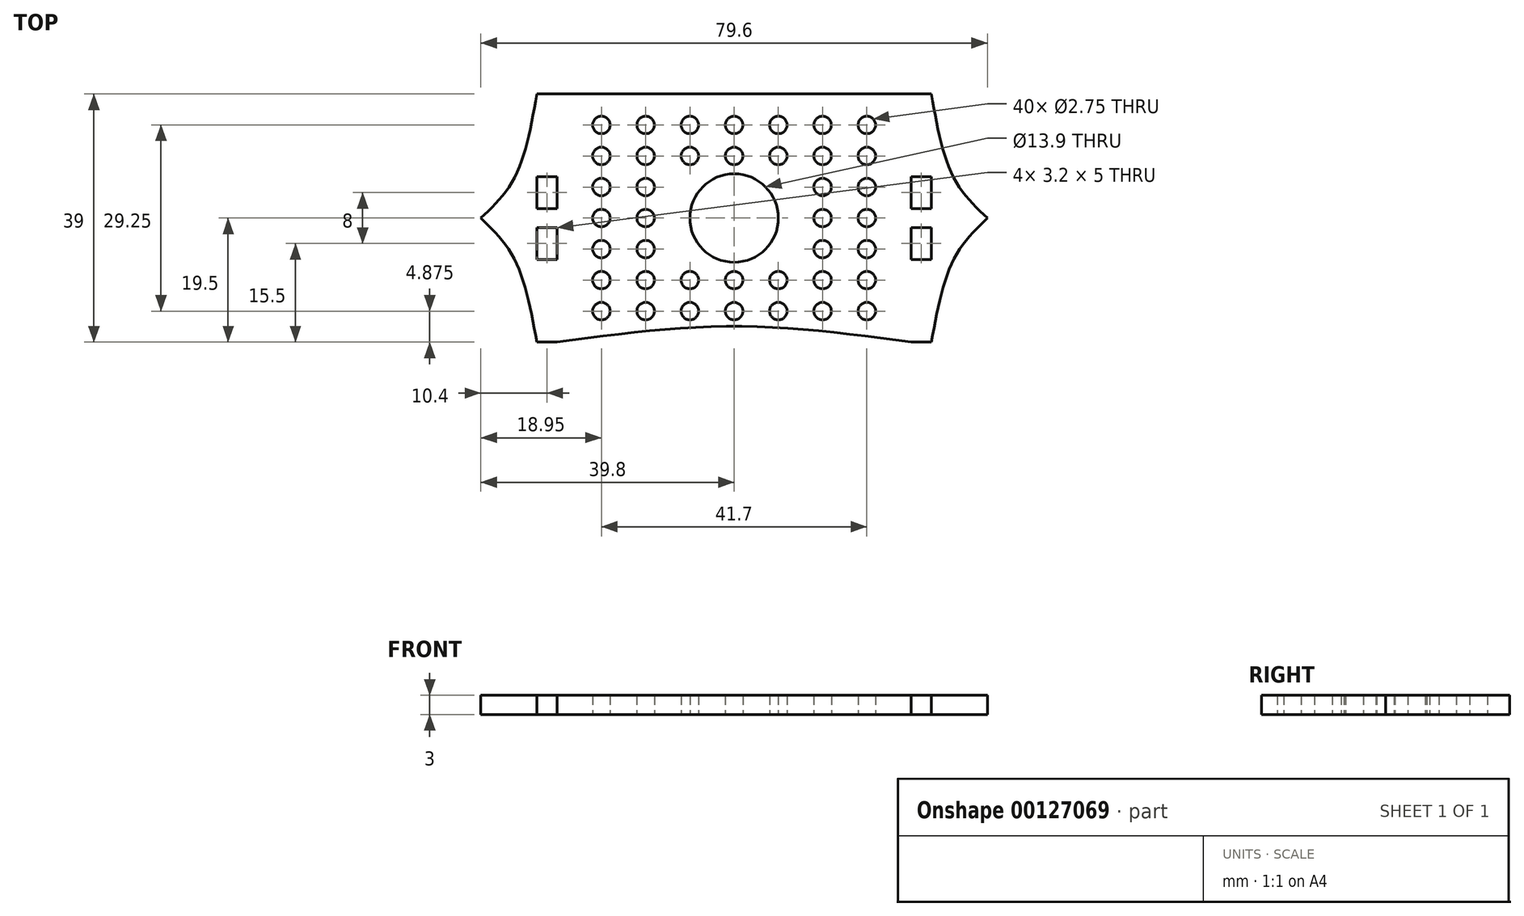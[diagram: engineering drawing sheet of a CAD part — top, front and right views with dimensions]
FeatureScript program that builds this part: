
annotation { "Feature Type Name" : "Feature", "Feature Type Description" : "" }
export const myFeature = defineFeature(function(context is Context, id is Id, definition is map)
    precondition{}
    {
        {
            var Q0;
            Q0=qCreatedBy(makeId("Top.planeOp"),FACE);
            var sketch = newSketch(context, id + "F0", { "sketchPlane" : qUnion([Q0])});
            skLineSegment(sketch, "E0", {"start": v(-27.8, -19.5) * mm, "end": v(-31, -19.5) * mm});
            skLineSegment(sketch, "E1", {"start": v(-27.8, -6.5) * mm, "end": v(-27.8, 1.84) * mm});
            skLineSegment(sketch, "E2", {"start": v(27.8, 6.5) * mm, "end": v(27.8, 3.3) * mm});
            skLineSegment(sketch, "E3", {"start": v(31, -19.5) * mm, "end": v(27.8, -19.5) * mm});
            skLineSegment(sketch, "E4", {"start": v(-27.8, -19.5) * mm, "end": v(-27.8, 1.84) * mm, "construction": true});
            skLineSegment(sketch, "E5", {"start": v(27.8, -19.5) * mm, "end": v(27.8, -3.3) * mm, "construction": true});
            skLineSegment(sketch, "E6", {"start": v(-27.8, 19.5) * mm, "end": v(-31, 19.5) * mm});
            skLineSegment(sketch, "E7", {"start": v(27.8, 19.5) * mm, "end": v(31, 19.5) * mm});
            skLineSegment(sketch, "E8", {"start": v(-31, -7) * mm, "end": v(-33.5, -7) * mm, "construction": true});
            skLineSegment(sketch, "E9", {"start": v(-27.8, 19.5) * mm, "end": v(27.8, 19.5) * mm});
            skFitSpline(sketch, "E10", {"points": [v(-27.8, -19.5) * mm, v(0, -17) * mm, v(27.8, -19.5) * mm], "startDerivative": vector(55.6, 7.5) * mm, "endDerivative": vector(55.6, -7.5) * mm});
            skLineSegment(sketch, "E11", {"start": v(-27.8, 19.5) * mm, "end": v(-13.9, 19.5) * mm, "construction": true});
            skLineSegment(sketch, "E12", {"start": v(-13.9, 19.5) * mm, "end": v(0, 19.5) * mm, "construction": true});
            skLineSegment(sketch, "E13", {"start": v(0, 19.5) * mm, "end": v(13.9, 19.5) * mm, "construction": true});
            skLineSegment(sketch, "E14", {"start": v(13.9, 19.5) * mm, "end": v(27.8, 19.5) * mm, "construction": true});
            skLineSegment(sketch, "E15", {"start": v(0, 19.5) * mm, "end": v(0, -17) * mm, "construction": true});
            skLineSegment(sketch, "E16", {"start": v(-27.8, 0) * mm, "end": v(27.8, 0) * mm, "construction": true});
            skLineSegment(sketch, "E17", {"start": v(-13.9, 19.5) * mm, "end": v(-13.9, -17.78) * mm, "construction": true});
            skLineSegment(sketch, "E18", {"start": v(13.9, 19.5) * mm, "end": v(13.9, -17.78) * mm, "construction": true});
            skLineSegment(sketch, "E19", {"start": v(20.85, 19.5) * mm, "end": v(20.85, -18.58) * mm, "construction": true});
            skLineSegment(sketch, "E20", {"start": v(6.95, 19.5) * mm, "end": v(6.95, -17.21) * mm, "construction": true});
            skLineSegment(sketch, "E21", {"start": v(-6.95, 19.5) * mm, "end": v(-6.95, -17.21) * mm, "construction": true});
            skLineSegment(sketch, "E22", {"start": v(-20.85, 19.5) * mm, "end": v(-20.85, -18.58) * mm, "construction": true});
            skCircle(sketch, "E23", {"center": v(0, 0) * mm, "radius": 6.95 * mm});
            skLineSegment(sketch, "E24", {"start": v(-27.8, 19.5) * mm, "end": v(-27.8, 9.75) * mm, "construction": true});
            skLineSegment(sketch, "E25", {"start": v(-27.8, 9.75) * mm, "end": v(27.8, 9.75) * mm, "construction": true});
            skLineSegment(sketch, "E26", {"start": v(-27.8, 0) * mm, "end": v(-27.8, -9.75) * mm, "construction": true});
            skLineSegment(sketch, "E27", {"start": v(-27.8, -9.75) * mm, "end": v(27.8, -9.75) * mm, "construction": true});
            skLineSegment(sketch, "E28", {"start": v(-27.8, 14.63) * mm, "end": v(27.8, 14.63) * mm, "construction": true});
            skLineSegment(sketch, "E29", {"start": v(-27.8, -4.88) * mm, "end": v(27.8, -4.87) * mm, "construction": true});
            skLineSegment(sketch, "E30", {"start": v(-27.8, 9.75) * mm, "end": v(-27.8, 4.88) * mm, "construction": true});
            skLineSegment(sketch, "E31", {"start": v(-27.8, 4.88) * mm, "end": v(27.8, 4.88) * mm, "construction": true});
            skLineSegment(sketch, "E32", {"start": v(-27.8, -9.75) * mm, "end": v(-27.8, -14.62) * mm, "construction": true});
            skLineSegment(sketch, "E33", {"start": v(-27.8, -14.62) * mm, "end": v(27.8, -14.62) * mm, "construction": true});
            skCircle(sketch, "E34", {"center": v(-20.85, -14.62) * mm, "radius": 1.38 * mm});
            skCircle(sketch, "E35", {"center": v(-13.9, -14.62) * mm, "radius": 1.38 * mm});
            skCircle(sketch, "E36", {"center": v(-6.95, -14.62) * mm, "radius": 1.38 * mm});
            skCircle(sketch, "E37", {"center": v(0, -14.62) * mm, "radius": 1.38 * mm});
            skCircle(sketch, "E38", {"center": v(-20.85, -9.75) * mm, "radius": 1.38 * mm});
            skCircle(sketch, "E39", {"center": v(-13.9, -9.75) * mm, "radius": 1.38 * mm});
            skCircle(sketch, "E40", {"center": v(-6.95, -9.75) * mm, "radius": 1.38 * mm});
            skCircle(sketch, "E41", {"center": v(0, -9.75) * mm, "radius": 1.38 * mm});
            skCircle(sketch, "E42", {"center": v(-20.85, -4.88) * mm, "radius": 1.38 * mm});
            skCircle(sketch, "E43", {"center": v(-13.9, -4.88) * mm, "radius": 1.38 * mm});
            skCircle(sketch, "E44", {"center": v(-20.85, 0) * mm, "radius": 1.38 * mm});
            skCircle(sketch, "E45", {"center": v(-13.9, 0) * mm, "radius": 1.38 * mm});
            skCircle(sketch, "E46.MirrorC", {"center": v(6.95, -9.75) * mm, "radius": 1.38 * mm});
            skCircle(sketch, "E47.MirrorC", {"center": v(20.85, -9.75) * mm, "radius": 1.38 * mm});
            skCircle(sketch, "E48.MirrorC", {"center": v(13.9, -14.62) * mm, "radius": 1.38 * mm});
            skCircle(sketch, "E49.MirrorC", {"center": v(13.9, -9.75) * mm, "radius": 1.38 * mm});
            skCircle(sketch, "E50.MirrorC", {"center": v(20.85, -14.62) * mm, "radius": 1.38 * mm});
            skCircle(sketch, "E51.MirrorC", {"center": v(6.95, -14.62) * mm, "radius": 1.38 * mm});
            skLineSegment(sketch, "E52.MirrorCS", {"start": v(27.8, -4.87) * mm, "end": v(-27.8, -4.88) * mm, "construction": true});
            skCircle(sketch, "E53.MirrorC", {"center": v(20.85, 0) * mm, "radius": 1.38 * mm});
            skCircle(sketch, "E54.MirrorC", {"center": v(20.85, -4.88) * mm, "radius": 1.38 * mm});
            skCircle(sketch, "E55.MirrorC", {"center": v(13.9, 0) * mm, "radius": 1.38 * mm});
            skCircle(sketch, "E56.MirrorC", {"center": v(13.9, -4.88) * mm, "radius": 1.38 * mm});
            skLineSegment(sketch, "E57.MirrorCS", {"start": v(27.8, 0) * mm, "end": v(-27.8, 0) * mm, "construction": true});
            skCircle(sketch, "E58.MirrorC", {"center": v(6.95, 14.62) * mm, "radius": 1.38 * mm});
            skCircle(sketch, "E59.MirrorC", {"center": v(-13.9, 14.63) * mm, "radius": 1.38 * mm});
            skCircle(sketch, "E60.MirrorC", {"center": v(20.85, 9.75) * mm, "radius": 1.38 * mm});
            skCircle(sketch, "E61.MirrorC", {"center": v(-13.9, 9.75) * mm, "radius": 1.38 * mm});
            skCircle(sketch, "E62.MirrorC", {"center": v(-20.85, 9.75) * mm, "radius": 1.38 * mm});
            skCircle(sketch, "E63.MirrorC", {"center": v(13.9, 9.75) * mm, "radius": 1.38 * mm});
            skCircle(sketch, "E64.MirrorC", {"center": v(13.9, 14.62) * mm, "radius": 1.38 * mm});
            skCircle(sketch, "E65.MirrorC", {"center": v(6.95, 9.75) * mm, "radius": 1.38 * mm});
            skCircle(sketch, "E66.MirrorC", {"center": v(20.85, 14.62) * mm, "radius": 1.38 * mm});
            skCircle(sketch, "E67.MirrorC", {"center": v(0, 9.75) * mm, "radius": 1.38 * mm});
            skCircle(sketch, "E68.MirrorC", {"center": v(-6.95, 9.75) * mm, "radius": 1.38 * mm});
            skCircle(sketch, "E69.MirrorC", {"center": v(-6.95, 14.63) * mm, "radius": 1.38 * mm});
            skCircle(sketch, "E70.MirrorC", {"center": v(-20.85, 14.63) * mm, "radius": 1.38 * mm});
            skCircle(sketch, "E71.MirrorC", {"center": v(0, 14.62) * mm, "radius": 1.38 * mm});
            skLineSegment(sketch, "E72.MirrorCS", {"start": v(27.8, 4.88) * mm, "end": v(-27.8, 4.87) * mm, "construction": true});
            skLineSegment(sketch, "E73.MirrorCS", {"start": v(20.85, -19.5) * mm, "end": v(20.85, 18.58) * mm, "construction": true});
            skLineSegment(sketch, "E74.MirrorCS", {"start": v(13.9, -19.5) * mm, "end": v(13.9, 17.78) * mm, "construction": true});
            skCircle(sketch, "E75.MirrorC", {"center": v(13.9, 4.88) * mm, "radius": 1.38 * mm});
            skCircle(sketch, "E76.MirrorC", {"center": v(20.85, 4.87) * mm, "radius": 1.38 * mm});
            skLineSegment(sketch, "E77.MirrorCS", {"start": v(-27.8, 4.87) * mm, "end": v(27.8, 4.88) * mm, "construction": true});
            skCircle(sketch, "E78.MirrorC", {"center": v(-20.85, 4.88) * mm, "radius": 1.38 * mm});
            skLineSegment(sketch, "E79.MirrorCS", {"start": v(-13.9, -19.5) * mm, "end": v(-13.9, 17.78) * mm, "construction": true});
            skLineSegment(sketch, "E80.MirrorCS", {"start": v(-20.85, -19.5) * mm, "end": v(-20.85, 18.58) * mm, "construction": true});
            skCircle(sketch, "E81.MirrorC", {"center": v(-13.9, 4.88) * mm, "radius": 1.38 * mm});
            skLineSegment(sketch, "E82", {"start": v(27.8, 0) * mm, "end": v(39.8, 0) * mm, "construction": true});
            skLineSegment(sketch, "E83", {"start": v(-27.8, 0) * mm, "end": v(-39.8, 0) * mm, "construction": true});
            skFitSpline(sketch, "E84", {"points": [v(39.8, 0) * mm, v(34.5, -6.5) * mm, v(31, -19.5) * mm], "startDerivative": vector(-13.28, -12.86) * mm, "endDerivative": vector(-4.65, -25.64) * mm, "construction": true});
            skLineSegment(sketch, "E85", {"start": v(34.42, 6.5) * mm, "end": v(31, 6.5) * mm, "construction": true});
            skFitSpline(sketch, "E86", {"points": [v(39.8, 0) * mm, v(34.42, 6.5) * mm, v(31, 19.5) * mm], "startDerivative": vector(-13.5, 12.8) * mm, "endDerivative": vector(-4.45, 25.7) * mm, "construction": true});
            skFitSpline(sketch, "E87", {"points": [v(31, 19.5) * mm, v(34.42, 6.5) * mm, v(39.8, 0) * mm], "startDerivative": vector(4.45, -25.7) * mm, "endDerivative": vector(13.5, -12.8) * mm});
            skFitSpline(sketch, "E88", {"points": [v(39.8, 0) * mm, v(34.5, -6.5) * mm, v(31, -19.5) * mm], "startDerivative": vector(-13.28, -12.86) * mm, "endDerivative": vector(-4.65, -25.64) * mm});
            skLineSegment(sketch, "E89", {"start": v(27.8, 6.5) * mm, "end": v(31, 6.5) * mm});
            skLineSegment(sketch, "E90", {"start": v(27.8, 3.3) * mm, "end": v(27.8, 6.5) * mm});
            skLineSegment(sketch, "E91", {"start": v(31, -6.5) * mm, "end": v(27.8, -6.5) * mm});
            skLineSegment(sketch, "E92", {"start": v(27.8, -6.5) * mm, "end": v(27.8, -3.3) * mm});
            skLineSegment(sketch, "E93", {"start": v(31, -3.3) * mm, "end": v(31, -6.5) * mm});
            skLineSegment(sketch, "E94.trimOffspring", {"start": v(27.8, 3.3) * mm, "end": v(27.8, 19.5) * mm, "construction": true});
            skLineSegment(sketch, "E95.trimOffspring", {"start": v(27.8, -4.87) * mm, "end": v(27.8, -6.5) * mm});
            skFitSpline(sketch, "E96.MirrorCS", {"points": [v(-39.8, 0) * mm, v(-34.42, 6.5) * mm, v(-31, 19.5) * mm], "startDerivative": vector(13.5, 12.8) * mm, "endDerivative": vector(4.45, 25.7) * mm, "construction": true});
            skLineSegment(sketch, "E97.MirrorCS", {"start": v(-31, -6.5) * mm, "end": v(-27.8, -6.5) * mm});
            skLineSegment(sketch, "E98.MirrorCS", {"start": v(-31, -3.3) * mm, "end": v(-31, -6.5) * mm});
            skLineSegment(sketch, "E99.MirrorCS", {"start": v(-27.8, 6.5) * mm, "end": v(-31, 6.5) * mm});
            skLineSegment(sketch, "E100.MirrorCS", {"start": v(-31, 6.5) * mm, "end": v(-31, 3.64) * mm});
            skFitSpline(sketch, "E101", {"points": [v(-31, 19.5) * mm, v(-34.42, 6.5) * mm, v(-39.8, 0) * mm], "startDerivative": vector(-4.45, -25.7) * mm, "endDerivative": vector(-13.5, -12.8) * mm});
            skFitSpline(sketch, "E102.MirrorCS", {"points": [v(-39.8, 0) * mm, v(-34.5, -6.5) * mm, v(-31, -19.5) * mm], "startDerivative": vector(13.28, -12.86) * mm, "endDerivative": vector(4.65, -25.64) * mm, "construction": true});
            skFitSpline(sketch, "E103", {"points": [v(-31, -19.5) * mm, v(-34.5, -6.5) * mm, v(-39.8, 0) * mm], "startDerivative": vector(-4.65, 25.64) * mm, "endDerivative": vector(-13.28, 12.86) * mm});
            skLineSegment(sketch, "E104", {"start": v(31, 6.5) * mm, "end": v(31, 1.5) * mm});
            skLineSegment(sketch, "E105", {"start": v(31, 1.5) * mm, "end": v(27.8, 1.5) * mm});
            skLineSegment(sketch, "E106", {"start": v(27.8, 1.5) * mm, "end": v(27.8, 3.3) * mm});
            skLineSegment(sketch, "E107", {"start": v(27.8, -3.3) * mm, "end": v(27.8, -1.5) * mm});
            skLineSegment(sketch, "E108", {"start": v(27.8, -1.5) * mm, "end": v(31, -1.5) * mm});
            skLineSegment(sketch, "E109", {"start": v(31, -1.5) * mm, "end": v(31, -3.3) * mm});
            skPoint(sketch, "E110.MirrorCS.end.orphan", {"position": v(-31, -3.3) * mm});
            skPoint(sketch, "E110.MirrorCS.start.orphan", {"position": v(-27.8, -3.3) * mm});
            skLineSegment(sketch, "E111", {"start": v(-31, -3.3) * mm, "end": v(-31, -1.5) * mm});
            skLineSegment(sketch, "E112", {"start": v(-31, -1.5) * mm, "end": v(-27.8, -1.5) * mm});
            skLineSegment(sketch, "E113", {"start": v(-27.8, -1.5) * mm, "end": v(-27.8, -3.3) * mm});
            skLineSegment(sketch, "E114.trimOffspring", {"start": v(-27.8, 9.75) * mm, "end": v(-27.8, 19.5) * mm, "construction": true});
            skLineSegment(sketch, "E115.trimOffspring", {"start": v(-27.8, 4.88) * mm, "end": v(-27.8, 6.5) * mm});
            skPoint(sketch, "E116.orphan", {"position": v(-27.8, 3.3) * mm});
            skLineSegment(sketch, "E117", {"start": v(-27.8, 6.5) * mm, "end": v(-27.8, 1.5) * mm});
            skLineSegment(sketch, "E118", {"start": v(-27.8, 1.5) * mm, "end": v(-31, 1.5) * mm});
            skLineSegment(sketch, "E119", {"start": v(-31, 1.5) * mm, "end": v(-31, 3.64) * mm});
            skSolve(sketch);
        }
        {
            var Q0;
            Q0=qSketchRegion(id+"F0",true);
            extrude(context, id + "F1", {"entities" : qUnion([Q0]), "endBound" : BoundingType.SYMMETRIC, "depth" : 3 * mm});
        }
    });
